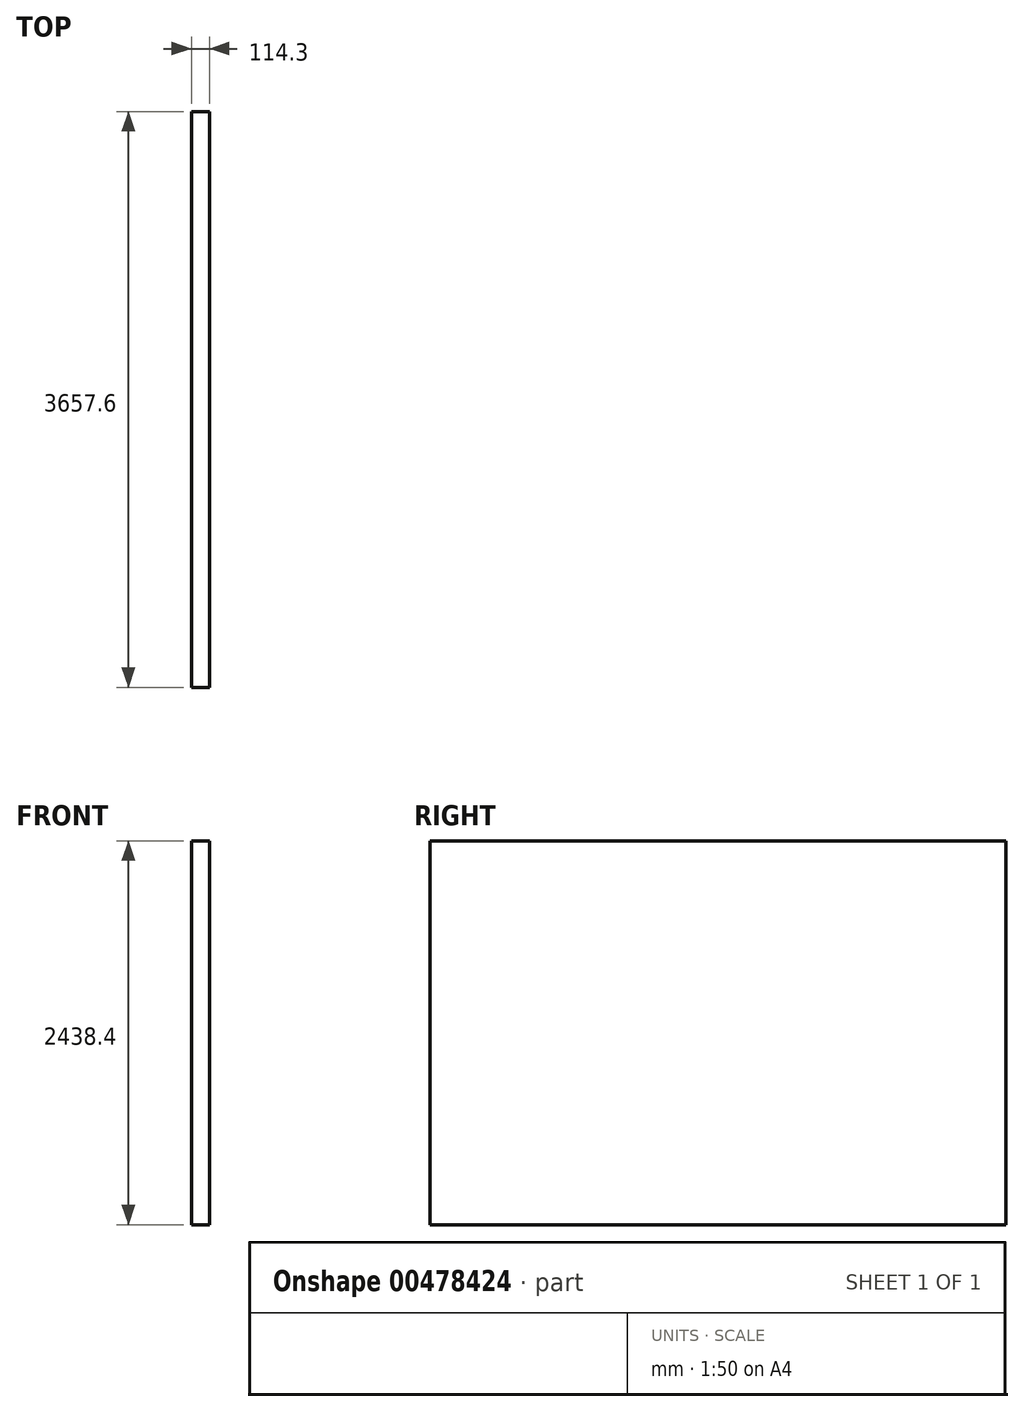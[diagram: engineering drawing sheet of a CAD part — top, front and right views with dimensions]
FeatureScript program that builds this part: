
annotation { "Feature Type Name" : "Feature", "Feature Type Description" : "" }
export const myFeature = defineFeature(function(context is Context, id is Id, definition is map)
    precondition{}
    {
        {
            var Q0;
            Q0=qCreatedBy(makeId("Top.planeOp"),FACE);
            var sketch = newSketch(context, id + "F0", { "sketchPlane" : qUnion([Q0])});
            skLineSegment(sketch, "E0.bottom", {"start": v(-57.15, 1828.8) * mm, "end": v(57.15, 1828.8) * mm});
            skLineSegment(sketch, "E0.top", {"start": v(-57.15, -1828.8) * mm, "end": v(57.15, -1828.8) * mm});
            skLineSegment(sketch, "E0.left", {"start": v(-57.15, 1828.8) * mm, "end": v(-57.15, -1828.8) * mm});
            skLineSegment(sketch, "E0.right", {"start": v(57.15, 1828.8) * mm, "end": v(57.15, -1828.8) * mm});
            skPoint(sketch, "E0.middle", {"position": v(0, 0) * mm});
            skSolve(sketch);
        }
        {
            var Q0;
            Q0 = qSketchRegion(id + "F0", true);
            extrude(context, id + "F1", {"entities" : qUnion([Q0]), "depth" : 2438.4 * mm});
        }
    });
